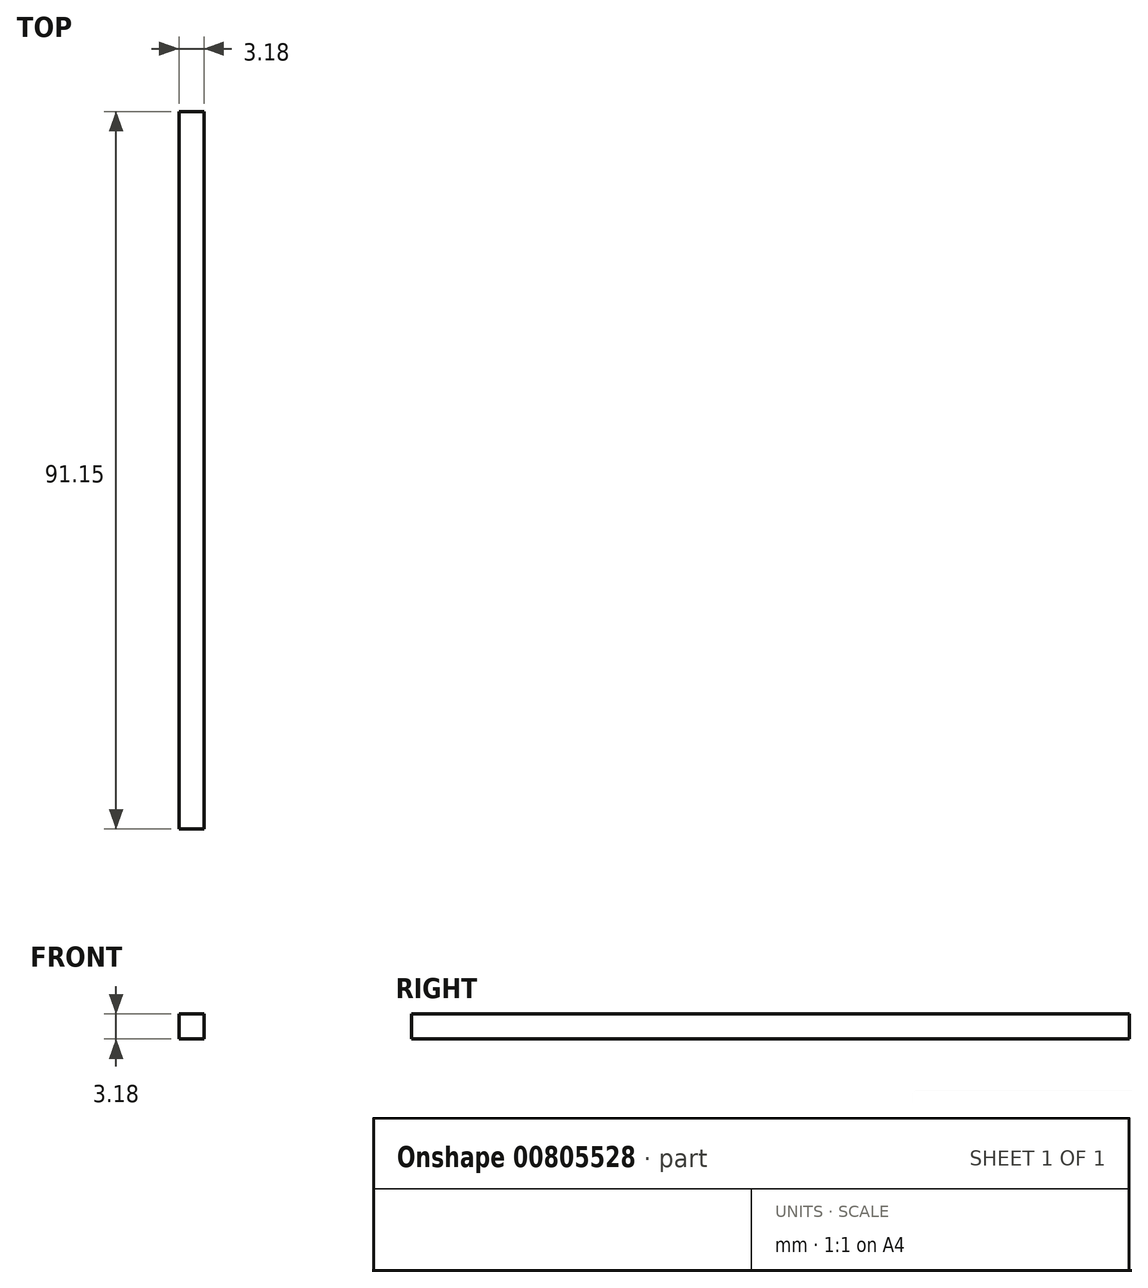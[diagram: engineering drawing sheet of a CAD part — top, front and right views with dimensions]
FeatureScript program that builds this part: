
annotation { "Feature Type Name" : "Feature", "Feature Type Description" : "" }
export const myFeature = defineFeature(function(context is Context, id is Id, definition is map)
    precondition{}
    {
        {
            var Q0;
            Q0=qCreatedBy(makeId("Front.planeOp"),FACE);
            var sketch = newSketch(context, id + "F0", { "sketchPlane" : qUnion([Q0])});
            skLineSegment(sketch, "E0.bottom", {"start": v(1.59, 1.59) * mm, "end": v(-1.59, 1.59) * mm});
            skLineSegment(sketch, "E0.top", {"start": v(1.59, -1.59) * mm, "end": v(-1.59, -1.59) * mm});
            skLineSegment(sketch, "E0.left", {"start": v(1.59, 1.59) * mm, "end": v(1.59, -1.59) * mm});
            skLineSegment(sketch, "E0.right", {"start": v(-1.59, 1.59) * mm, "end": v(-1.59, -1.59) * mm});
            skPoint(sketch, "E0.middle", {"position": v(0, 0) * mm});
            skSolve(sketch);
        }
        {
            var Q0;
            Q0=makeQuery(id+"F0.imprint","IMPRINT",FACE,{"disambiguationData":[TD([[makeQuery(id+"F0.imprint","IMPRINT",EDGE,{"derivedFrom":sQuery(id+"F0.wireOp",EDGE,"E0.bottom")}),1.0]])]});
            extrude(context, id + "F1", {"entities" : qUnion([Q0]), "depth" : 91.15 * mm, "offsetDistance" : 25 * mm});
        }
    });
